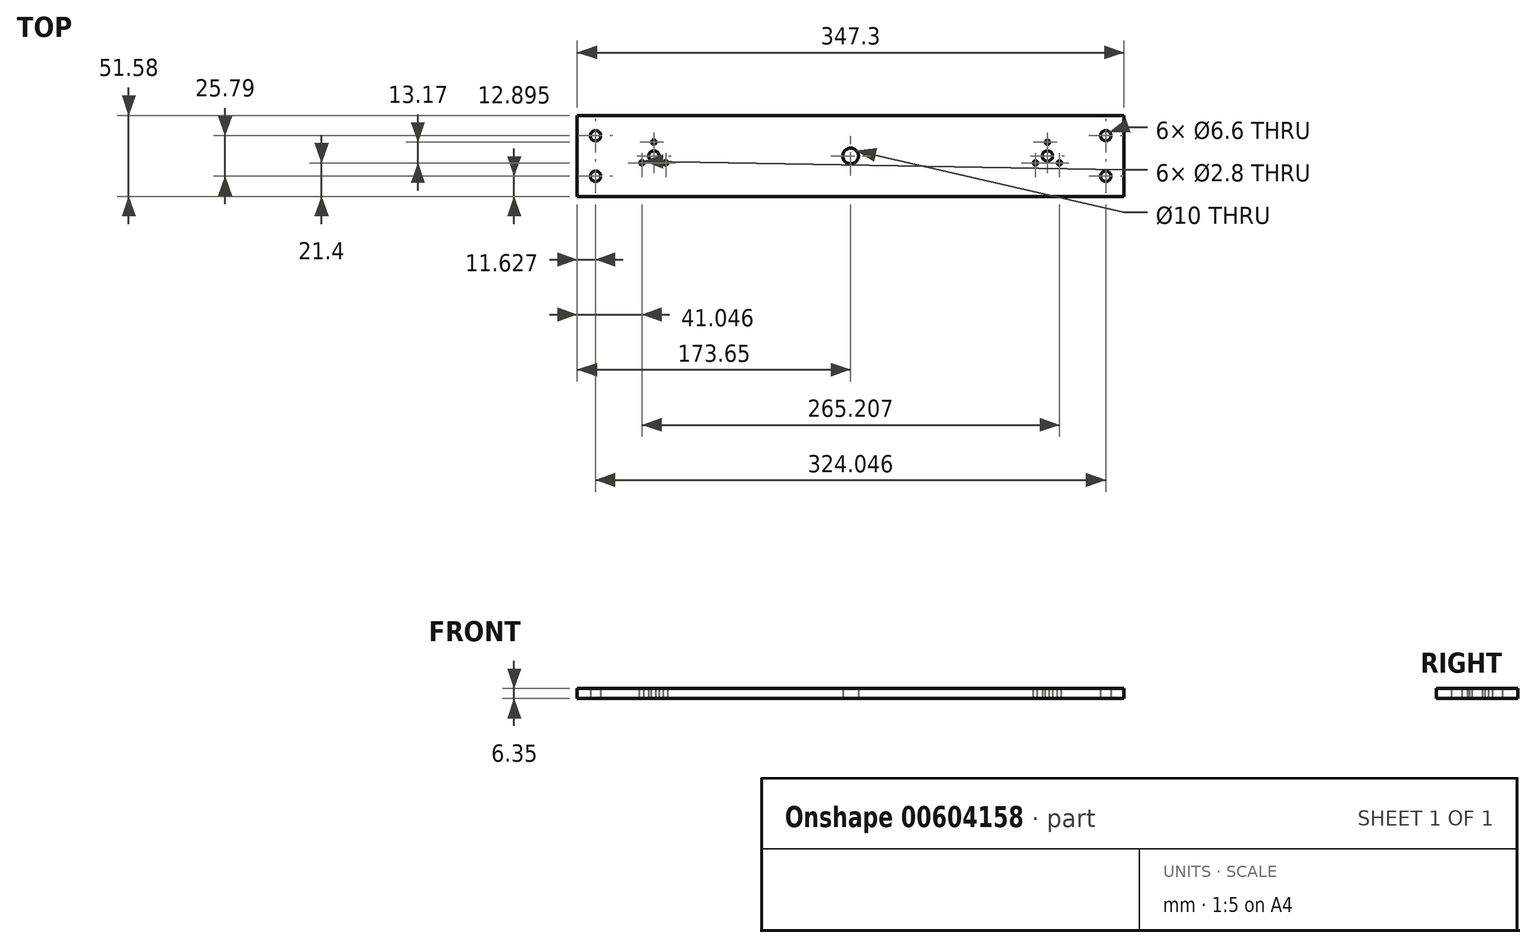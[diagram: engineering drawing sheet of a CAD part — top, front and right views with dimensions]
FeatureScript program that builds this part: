
annotation { "Feature Type Name" : "Feature", "Feature Type Description" : "" }
export const myFeature = defineFeature(function(context is Context, id is Id, definition is map)
    precondition{}
    {
        {
            var Q0;
            Q0=qCreatedBy(makeId("Top.planeOp"),FACE);
            var sketch = newSketch(context, id + "F0", { "sketchPlane" : qUnion([Q0])});
            skLineSegment(sketch, "E0.bottom", {"start": v(173.65, 25.79) * mm, "end": v(-173.65, 25.8) * mm});
            skLineSegment(sketch, "E0.top", {"start": v(173.65, -25.8) * mm, "end": v(-173.65, -25.79) * mm});
            skLineSegment(sketch, "E0.left", {"start": v(173.65, 25.79) * mm, "end": v(173.65, -25.8) * mm});
            skLineSegment(sketch, "E0.right", {"start": v(-173.65, 25.8) * mm, "end": v(-173.65, -25.8) * mm});
            skPoint(sketch, "E0.middle", {"position": v(0, 0) * mm});
            skLineSegment(sketch, "E1", {"start": v(-173.65, 0) * mm, "end": v(173.65, 0) * mm, "construction": true});
            skPoint(sketch, "E2", {"position": v(-125, 0) * mm});
            skPoint(sketch, "E3", {"position": v(125, 0) * mm});
            skCircle(sketch, "E4", {"center": v(-125, 0) * mm, "radius": 3.3 * mm});
            skCircle(sketch, "E5", {"center": v(0, 0) * mm, "radius": 5 * mm});
            skCircle(sketch, "E6", {"center": v(125, 0) * mm, "radius": 3.3 * mm});
            skSolve(sketch);
        }
        {
            var Q0;
            Q0 = qSketchRegion(id + "F0", true);
            extrude(context, id + "F1", {"entities" : qUnion([Q0]), "depth" : 6.35 * mm, "offsetDistance" : 25 * mm});
        }
        {
            var Q0;
            Q0=makeQuery(id+"F1.opExtrude","CAP_FACE",FACE,{"disambiguationData":[OSD([sQuery(id+"F0.wireOp",EDGE,"E0.bottom"),sQuery(id+"F0.wireOp",EDGE,"E0.top"),sQuery(id+"F0.wireOp",EDGE,"E0.left"),sQuery(id+"F0.wireOp",EDGE,"E0.right"),sQuery(id+"F0.wireOp",EDGE,"E4"),sQuery(id+"F0.wireOp",EDGE,"E5"),sQuery(id+"F0.wireOp",EDGE,"E6")])],"isStart":true});
            var sketch = newSketch(context, id + "F2", { "sketchPlane" : qUnion([Q0])});
            skLineSegment(sketch, "E7", {"start": v(-173.65, 0) * mm, "end": v(173.65, 0) * mm, "construction": true});
            skLineSegment(sketch, "E8", {"start": v(-173.65, 0) * mm, "end": v(-173.65, 25.8) * mm, "construction": true});
            skLineSegment(sketch, "E9", {"start": v(-173.65, 0) * mm, "end": v(-173.65, -25.8) * mm, "construction": true});
            skLineSegment(sketch, "E10", {"start": v(-173.65, 12.9) * mm, "end": v(-162.02, 12.9) * mm, "construction": true});
            skLineSegment(sketch, "E11", {"start": v(-173.65, -12.9) * mm, "end": v(-162.02, -12.9) * mm, "construction": true});
            skLineSegment(sketch, "E12", {"start": v(173.65, 0) * mm, "end": v(173.65, 25.8) * mm, "construction": true});
            skLineSegment(sketch, "E13", {"start": v(173.65, 0) * mm, "end": v(173.65, -25.79) * mm, "construction": true});
            skLineSegment(sketch, "E14", {"start": v(0, 25.8) * mm, "end": v(0, -25.8) * mm, "construction": true});
            skLineSegment(sketch, "E15.MirrorCS", {"start": v(173.65, 12.9) * mm, "end": v(162.02, 12.9) * mm, "construction": true});
            skLineSegment(sketch, "E16.MirrorCS", {"start": v(173.65, -12.9) * mm, "end": v(162.02, -12.9) * mm, "construction": true});
            skSolve(sketch);
        }
        {
            var Q0;
            Q0=sQuery(id+"F2.wireOp",VERTEX,"E10.end");
            var Q1;
            Q1=sQuery(id+"F2.wireOp",VERTEX,"E11.end");
            var Q2;
            Q2=sQuery(id+"F2.wireOp",VERTEX,"iHLwx6hD-fz6N-HCwB-JFHI-69YMOSLrgtbU.end");
            var Q3;
            Q3=sQuery(id+"F2.wireOp",VERTEX,"2NG1YTGv-0bZk-gzUh-olJz-pQPr3KuJQsRM.end");
            var Q4;
            Q4=sQuery(id+"F2.wireOp",VERTEX,"E16.MirrorCS.end");
            var Q5;
            Q5=sQuery(id+"F2.wireOp",VERTEX,"E15.MirrorCS.end");
            var Q6;
            Q6=makeQuery(id+"F1.opExtrude","SWEPT_BODY",BODY,{"disambiguationData":[OSD([sQuery(id+"F0.wireOp",EDGE,"E0.bottom"),sQuery(id+"F0.wireOp",EDGE,"E0.top"),sQuery(id+"F0.wireOp",EDGE,"E0.left"),sQuery(id+"F0.wireOp",EDGE,"E0.right"),sQuery(id+"F0.wireOp",EDGE,"E4"),sQuery(id+"F0.wireOp",EDGE,"E5"),sQuery(id+"F0.wireOp",EDGE,"E6")])]});
            hole(context, id + "F3", {"style" : HoleStyle.SIMPLE, "endStyle" : HoleEndStyle.THROUGH, "standardTappedOrClearance" : lookupTablePath({ "standard" : "ISO", "fit" : "Normal", "size" : "M6", "type" : "Clearance" }), "standardBlindInLast" : lookupTablePath({ "fit" : "Standard", "standard" : "ISO", "size" : "M6", "type" : "Clearance" }), "holeDiameter" : 6.6 * mm, "majorDiameter" : 5 * mm, "isTappedThrough" : true, "tappedDepth" : 12 * mm, "tapClearance" : 3, "locations" : qUnion([Q0, Q1, Q2, Q3, Q4, Q5]), "scope" : qUnion([Q6])});
        }
        {
            var Q0;
            Q0=makeQuery(id+"F1.opExtrude","CAP_FACE",FACE,{"disambiguationData":[OSD([sQuery(id+"F0.wireOp",EDGE,"E0.bottom"),sQuery(id+"F0.wireOp",EDGE,"E0.top"),sQuery(id+"F0.wireOp",EDGE,"E0.left"),sQuery(id+"F0.wireOp",EDGE,"E0.right"),sQuery(id+"F0.wireOp",EDGE,"E4"),sQuery(id+"F0.wireOp",EDGE,"E5"),sQuery(id+"F0.wireOp",EDGE,"E6")])],"isStart":false});
            var sketch = newSketch(context, id + "F4", { "sketchPlane" : qUnion([Q0])});
            skLineSegment(sketch, "E17", {"start": v(-173.65, 0) * mm, "end": v(173.65, 0) * mm, "construction": true});
            skCircle(sketch, "E18", {"center": v(-125, 0) * mm, "radius": 8.78 * mm, "construction": true});
            skCircle(sketch, "E19", {"center": v(125, 0) * mm, "radius": 8.78 * mm, "construction": true});
            skCircle(sketch, "E20", {"center": v(-125, 8.78) * mm, "radius": 1.4 * mm});
            skCircle(sketch, "E21.1.0", {"center": v(-132.6, -4.4) * mm, "radius": 1.4 * mm});
            skCircle(sketch, "E21.2.0", {"center": v(-117.4, -4.4) * mm, "radius": 1.4 * mm});
            skCircle(sketch, "E22.MirrorC", {"center": v(125, 8.78) * mm, "radius": 1.4 * mm});
            skCircle(sketch, "E23.MirrorC", {"center": v(132.6, -4.39) * mm, "radius": 1.4 * mm});
            skCircle(sketch, "E24.MirrorC", {"center": v(117.4, -4.39) * mm, "radius": 1.4 * mm});
            skSolve(sketch);
        }
        {
            var Q0;
            Q0 = qSketchRegion(id + "F4", true);
            extrude(context, id + "F5", {"entities" : qUnion([Q0]), "operationType" : NewBodyOperationType.REMOVE, "endBound" : BoundingType.THROUGH_ALL, "oppositeDirection" : true, "depth" : 25 * mm, "offsetDistance" : 25 * mm});
        }
    });
